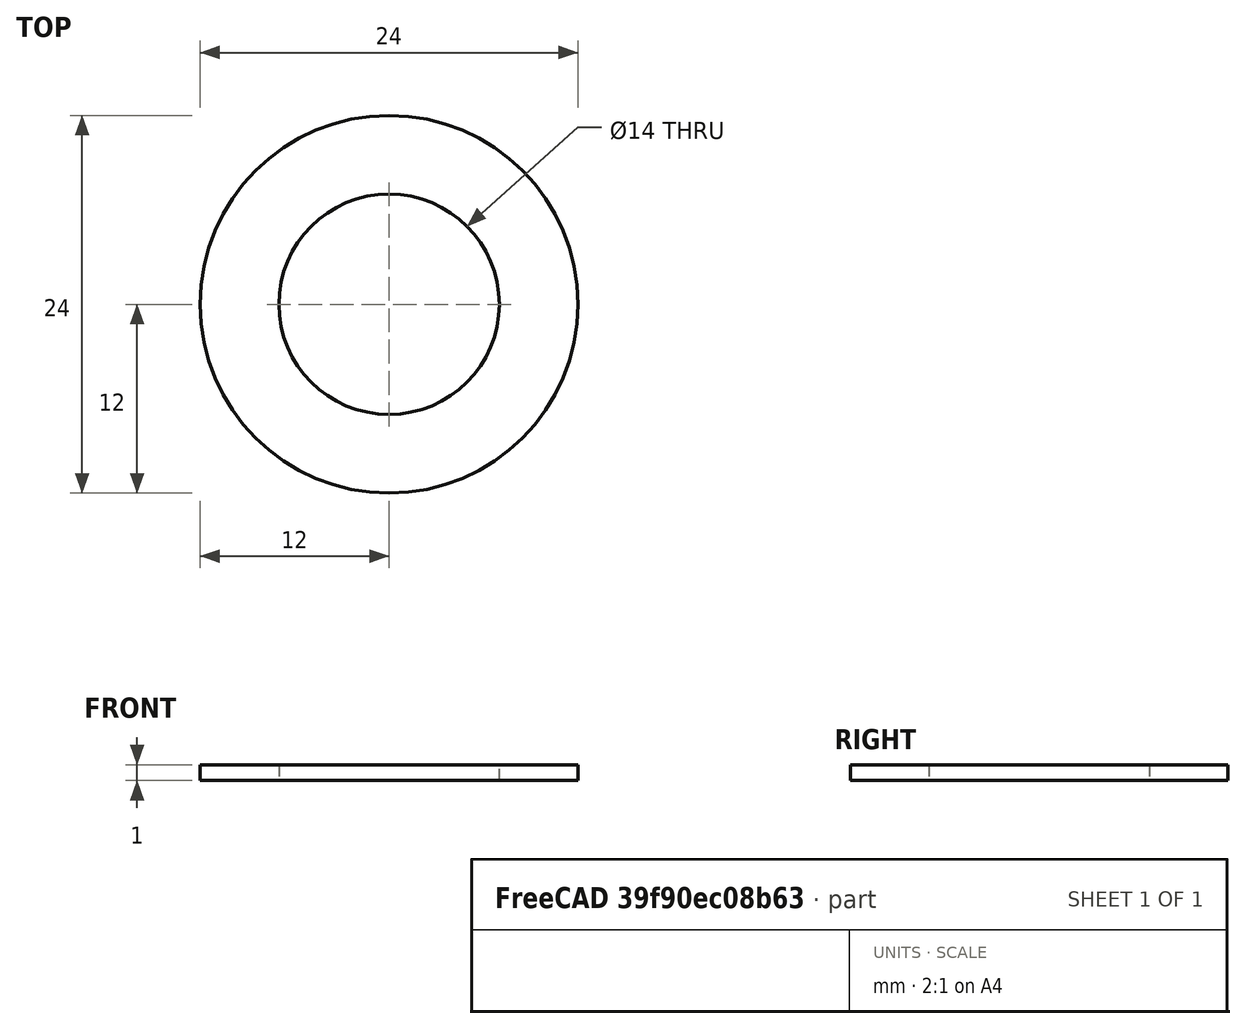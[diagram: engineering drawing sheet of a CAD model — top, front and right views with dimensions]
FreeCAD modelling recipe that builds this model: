
FCSTD DOCUMENT  (FreeCAD 0.19R24276 (Git))
Label: Seal_turning_ring_d14_d24_h1
License: All rights reserved
LicenseURL: http://en.wikipedia.org/wiki/All_rights_reserved
objects: Sketcher::SketchObject×1, PartDesign::Pad×1, PartDesign::Body×1
note: 4 computed .brp shape members not serialized (recipe doc carries the construction recipe); baked Part::Feature solids carry a one-line shape summary decoded from their .brp

FEATURE [Sketcher::SketchObject] Sketch  label="Sketch_d14_d24"
  FullyConstrained = true
  MapMode = 5
  Support = -> [XY_Plane]
  sketch-geometry (2):
    g0: Circle CenterX=0 CenterY=0 CenterZ=0 NormalX=0 NormalY=0 NormalZ=1 AngleXU=0 Radius=12
    g1: Circle CenterX=0 CenterY=0 CenterZ=0 NormalX=0 NormalY=0 NormalZ=1 AngleXU=0 Radius=7
  constraints (4):
    c: Coincident(g0,g-1)
    c: Coincident(g1,g0)
    c: Diameter(g0) = 24
    c: Diameter(g1) = 14
FEATURE [PartDesign::Pad] Pad
  Direction = (1,1,1)
  Length = 1
  Length2 = 100
  Profile = -> Sketch
  Type = 0
FEATURE [PartDesign::Body] Body
  Group = -> [Sketch,Pad]
  Origin = -> Origin
  Tip = -> Pad
